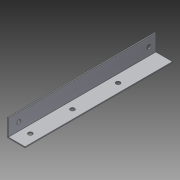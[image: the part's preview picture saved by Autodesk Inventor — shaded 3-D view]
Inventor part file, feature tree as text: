
AUTODESK INVENTOR PART (.ipt)
format: ipt  version: 2014 SP1 (Build 180222100, 222)  size: 99,328 bytes
history: native  units: in
note: dims shown in document units (in); Inventor stores cm internally (conversion verified against a paired STEP export)
features: extrude x3, sketch x3
ambient origin geometry x8: Origin, YZ Plane, XZ Plane, XY Plane, X Axis, Y Axis, Z Axis, Center Point
bodies: Solid1 (feature_tree)
feature tree (6):
  extrude  "Extrusion1"  Depth=0.0312in
  extrude  "Extrusion2"  Depth=5.25in
  extrude  "Extrusion3"  Depth=1.625in
  sketch  "Sketch1"  dims[d0=0.625in d1=0.0312in]
  sketch  "Sketch2"  dims[d2=5.25in d3=0.0in d4=0.15in]
  sketch  "Sketch3"  dims[d6=0.5in d7=1.625in d8=1.0in d9=0.0in d11=0.15in d12=0.375in d13=0.25in d14=1.0in d15=0.0in d16=1.5in]
